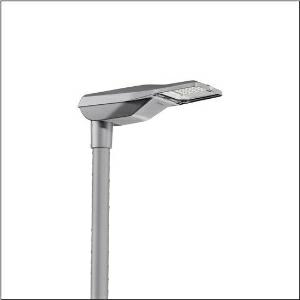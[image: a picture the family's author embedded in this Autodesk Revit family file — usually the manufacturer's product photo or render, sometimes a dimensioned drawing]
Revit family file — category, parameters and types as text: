
# Revit family: streetlight_sl_21_iq_micro___stw1_0a_5xe1e31d08db_99ec
name_source: partatom
category: Lighting Fixtures
units: mm (PartAtom-declared; Revit-internal decimal feet)

## family parameters
Cut with Voids When Loaded = No
Host = Face
Light Source = No
Part Type = Normal
Room Calculation Point = No
Round Connector Dimension = Use Diameter
Shared = No

## types (1)
- --- (1 x LED, 4810 lm, 36.4 W, 3000K)
    Apparent Load = 36 VA
    CIE Flux Codes = 38 75 98 100 100
    Color Rendering = 70
    Color Temperature = 3000K
    Default Elevation = 1800 mm
    Description = Streetlight SL 21 iQ micro, mast luminaire, primary light control with lens, of PMMA, primary optical cover: cover, of toughened safety glass, transparent, light distribution: STW1.0a, light emission: direct distribution, primary light characteristic: asymmetric, installation type: post-top, side-entry, LED, High Power LED, rated luminous flux: 4.810lm, luminous efficacy: 132lm/W, light colour: 730, colour temperature: 3000K, control gear: iQ-Comfort, control: Auto-Match, Temp-Guard, Lumen-Switch, Night-Set, Smart-Wire, Light-Fading, Desk-Remote (wireless, voltage-free reading and setting of iQ features in the workshop via application-optimized NFC function/RFID function), optimised constant luminous flux control (CLO 2.0), pre-setting: linear dimming characteristic, mains connection: 220..240V, AC, 50/60Hz, start of lifetime: 36W, end of service life: 38W, reduction: 16W, luminaire housing, of diecast aluminium, powder-coated, Siteco® metallic grey (DB 702S), corrosivity category C5 mid according to DIN EN ISO 12944, please order mast flange separately, inclination adjustable: 0°, 5°, 10°, 15°, sealing non-destructively replaceable, multi-level sealing system, length: 528mm, width: 235mm, height: 110mm, mast flange for spigot size: 42mm (side-entry): 5XC10008XM4, 60/48mm (side-entry/post-top): 5XC10108XM2, 76/60mm (side-entry/post-top): 5XC10108XM1, protection rating (complete): IP66, insulation class (complete): insulation class II (safety insulation), certification: CE, ENEC, ENEC+, VDE, impact resistance: IK10, permissible operating ambient temperature for outdoor applications: -40..+50°C, standard-compliant lighting for roads and squares, packaging unit: 1 piece

Light Distribution: STW1.0a
    Height = 110 mm
    Lamp = 1 x LED
    Lamp Light Flux = 4810 lm
    Lamp Power = 36.4 W
    Lamp count = 1
    Length = 528 mm
    Luminous efficacy = 132 lm/W
    Manufacturer = Siteco
    ModVariant = No
    Model = 5XE1E31D08DB
    Number of Poles = 1
    OnlyDefault = Yes
    Power Factor = 1
    Product Name = Streetlight SL 21 iQ micro | STW1.0a
    Product group = mast luminaire | pylon top
    ProductGroupID = 6100
    Protection Class = Protection class II
    Protection Degree = IP 66
    RLX_Detail_Level = 1
    RLX_Emergency_Light_Flux = 0 lm
    RLX_Emergency_Type = 0
    RLX_Emergency_Type_DB = No
    RlxData = <blob elided: 98849 chars, md5=318c78a7>
    Socket = socket
    Standby Power = 0 W
    System Light Flux = 4810 lm
    System Power = 36 W
    Type Comments = factory setting: luminous flux: 100 % | dim-lin: 254 | 715 mA
    Type Image = l_1006881.jpg
    URL = http://relux.com
    VarID = @adj_155538
    Voltage = 0 V
    Weight = 0.00 kg
    Width = 235 mm

## geometry (parser evidence)
native form markers: Blend x4, Sweep x10
no freeform markers — native parametric forms only
